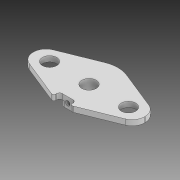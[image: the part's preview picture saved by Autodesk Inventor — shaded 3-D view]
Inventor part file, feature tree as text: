
AUTODESK INVENTOR PART (.ipt)
format: ipt  version: 2020 (Build 240168000, 168)  size: 377,856 bytes
history: native  units: mm
features: sketch x14, extrude x13, other x7, revolve x2, fillet x2, projected_geometry x2, imported_body x1
ambient origin geometry x8: Origin, YZ Plane, XZ Plane, XY Plane, X Axis, Y Axis, Z Axis, Center Point
bodies: Solid1 (feature_tree)
feature tree (41):
  other  "HD_mastersketch.ipt"
  other  "Blocks"
  revolve  "Revolution1"  [1 undecoded]
  extrude  "Extrusion1"  Depth=10.0mm
  extrude  "Extrusion2"  TaperAngle=0.0deg  [1 undecoded]
  fillet  "Fillet1"  [1 undecoded]
  extrude  "Extrusion3"  Depth=7.0mm
  revolve  "Revolution2"  [1 undecoded]
  extrude  "Extrusion7"  Depth=1.65mm
  extrude  "Extrusion8"  Depth=10.0mm
  extrude  "Extrusion9"  TaperAngle=90.0deg  [1 undecoded]
  extrude  "Extrusion10"  Depth=10.0mm TaperAngle=0.0deg
  extrude  "Extrusion11"  Depth=10.0mm TaperAngle=0.0deg
  extrude  "Extrusion16"  Depth=1.0mm TaperAngle=0.0deg
  extrude  "Extrusion12"  Depth=3.25mm TaperAngle=0.0deg
  extrude  "Extrusion13"  Depth=3.25mm TaperAngle=0.0deg
  extrude  "Extrusion14"  TaperAngle=0.0deg  [1 undecoded]
  extrude  "Extrusion15"  Depth=1.0mm
  fillet  "Fillet4"  Radius=8.05mm
  other  "608 bearing"
  other  "Belt"
  other  "Rotor"
  imported_body  "Base"
  sketch  "Sketch8"  dims[d1=10.0mm d24=7.0mm d25=22.0mm d26=8.0mm]
  sketch  "Sketch9"  dims[d2=90.0deg d3=5.0mm d4=10.0mm]
  sketch  "Sketch10"  dims[d5=15.0mm d6=0.0mm d7=0.0mm d8=0.0mm d9=0.0mm]
  sketch  "Sketch14"  dims[d10=7.0mm d11=3.6mm]
  sketch  "Sketch15"  dims[d12=2.3mm d13=5.7mm]
  sketch  "Sketch16"  dims[d14=5.7mm d15=0.0mm d29=1.65mm]
  sketch  "Sketch17"  dims[d30=3.0mm d32=10.0mm]
  sketch  "Sketch18"  dims[d33=1.5mm d34=90.0deg]
  sketch  "Sketch20"  dims[d36=4.0mm d38=10.0mm d39=0.0mm]
  projected_geometry  "Projected Loop1"
  sketch  "Sketch21"  dims[d40=10.0mm d41=0.0mm d42=10.0mm d43=0.0mm]
  sketch  "Sketch22"  dims[d44=1.0mm d45=0.0mm d47=1.0mm d48=0.0mm]
  projected_geometry  "Projected Loop2"
  sketch  "Sketch23"  dims[d49=2.0mm d50=2.25mm d51=0.0mm d52=0.0mm d53=3.25mm d54=0.0mm]
  sketch  "Sketch24"  dims[d55=2.5mm d56=3.25mm d57=0.0mm]
  sketch  "Sketch26"  dims[d58=1.5625mm d59=0.0mm d60=0.0mm d61=1.0mm d62=1.5625mm d63=8.05mm d64=10.0mm d65=0.0mm]
  other  "608 bearing:1"
  other  "608 bearing:2"
note: 6 required parameter values undecoded (feature->parameter linkage not recoverable at this tier; creation-order binding heuristic only, values carry confidence <= 0.55)